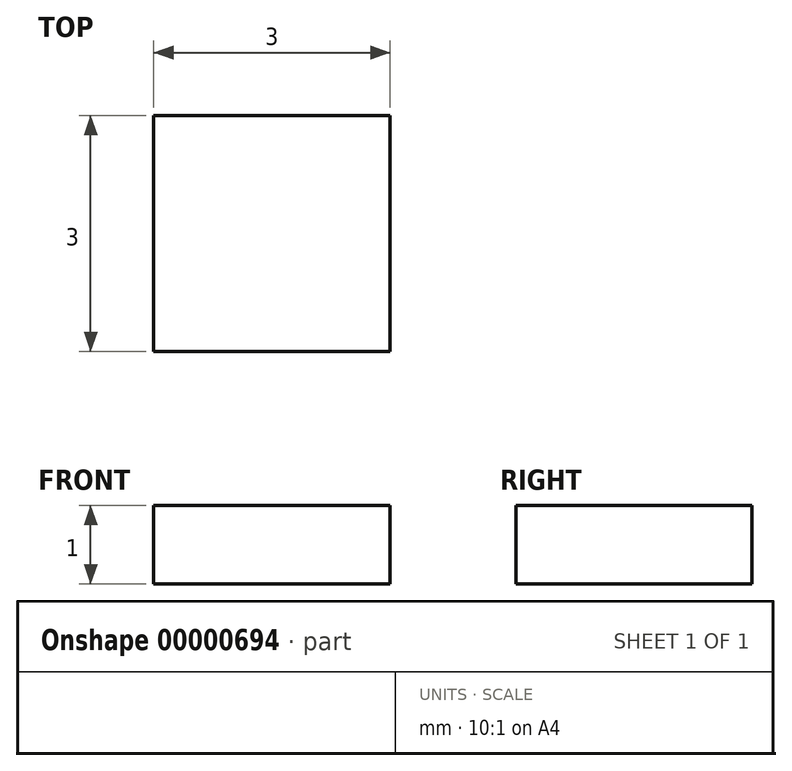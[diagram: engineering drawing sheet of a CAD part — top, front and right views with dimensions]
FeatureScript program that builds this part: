
annotation { "Feature Type Name" : "Feature", "Feature Type Description" : "" }
export const myFeature = defineFeature(function(context is Context, id is Id, definition is map)
    precondition{}
    {
        {
            var Q0;
            Q0=qCreatedBy(makeId("Top.planeOp"),FACE);
            var sketch = newSketch(context, id + "F0", { "sketchPlane" : qUnion([Q0])});
            skLineSegment(sketch, "E0.bottom", {"start": v(0, 0) * mm, "end": v(3, 0) * mm});
            skLineSegment(sketch, "E0.top", {"start": v(0, 3) * mm, "end": v(3, 3) * mm});
            skLineSegment(sketch, "E0.left", {"start": v(0, 0) * mm, "end": v(0, 3) * mm});
            skLineSegment(sketch, "E0.right", {"start": v(3, 0) * mm, "end": v(3, 3) * mm});
            skSolve(sketch);
        }
        {
            var Q0;
            Q0=makeQuery(id+"F0.imprint","IMPRINT",FACE,{"disambiguationData":[TD([[makeQuery(id+"F0.imprint","IMPRINT",EDGE,{"derivedFrom":sQuery(id+"F0.wireOp",EDGE,"E0.bottom")}),1.0]])]});
            extrude(context, id + "F1", {"entities" : qUnion([Q0]), "depth" : 1 * mm});
        }
    });
